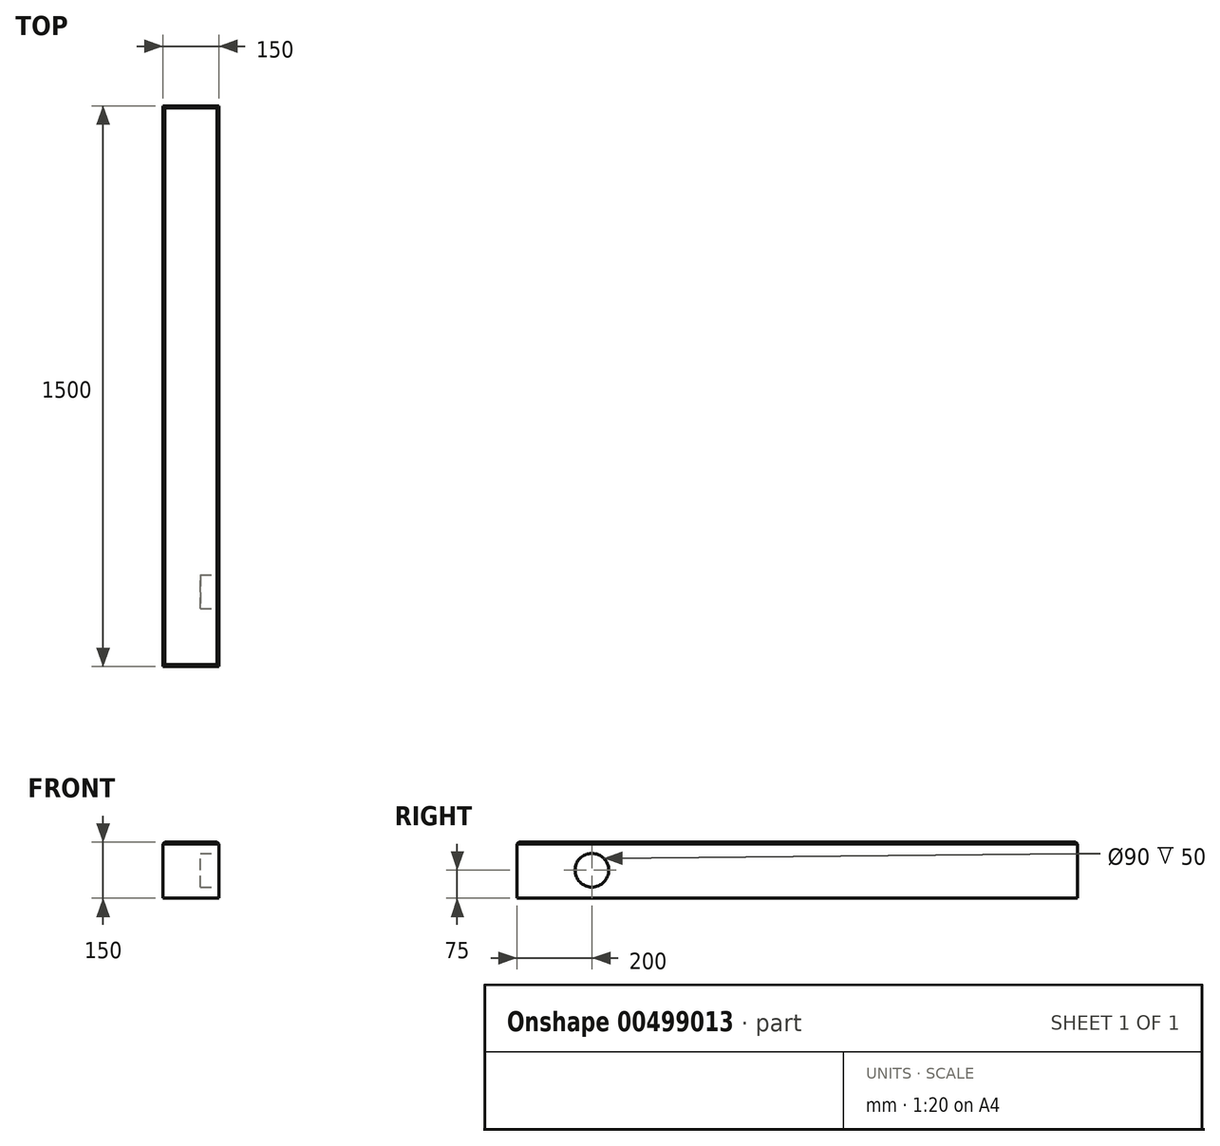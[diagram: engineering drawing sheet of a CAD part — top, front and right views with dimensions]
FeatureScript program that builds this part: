
annotation { "Feature Type Name" : "Feature", "Feature Type Description" : "" }
export const myFeature = defineFeature(function(context is Context, id is Id, definition is map)
    precondition{}
    {
        {
            var Q0;
            Q0=qCreatedBy(makeId("Front.planeOp"),FACE);
            var sketch = newSketch(context, id + "F0", { "sketchPlane" : qUnion([Q0])});
            skLineSegment(sketch, "E0.bottom", {"start": v(-75, 75) * mm, "end": v(75, 75) * mm});
            skLineSegment(sketch, "E0.top", {"start": v(-75, -75) * mm, "end": v(75, -75) * mm});
            skLineSegment(sketch, "E0.left", {"start": v(-75, 75) * mm, "end": v(-75, -75) * mm});
            skLineSegment(sketch, "E0.right", {"start": v(75, 75) * mm, "end": v(75, -75) * mm});
            skPoint(sketch, "E0.middle", {"position": v(0, 0) * mm});
            skSolve(sketch);
        }
        {
            var Q0;
            Q0 = qSketchRegion(id + "F0", true);
            extrude(context, id + "F1", {"entities" : qUnion([Q0]), "endBound" : BoundingType.SYMMETRIC, "depth" : 1500 * mm});
        }
        {
            var Q0;
            Q0=makeQuery(id+"F1.opExtrude","SWEPT_FACE",FACE,{"disambiguationData":[OSD([sQuery(id+"F0.wireOp",EDGE,"E0.bottom")])]});
            chamfer(context, id + "F2", {"entities" : qUnion([Q0]), "width" : 5 * mm, "tangentPropagation" : true});
        }
        {
            var Q0;
            Q0=makeQuery(id+"F1.opExtrude","SWEPT_FACE",FACE,{"disambiguationData":[OSD([sQuery(id+"F0.wireOp",EDGE,"E0.right")])]});
            var sketch = newSketch(context, id + "F3", { "sketchPlane" : qUnion([Q0])});
            skCircle(sketch, "E1", {"center": v(-550, 0) * mm, "radius": 45 * mm});
            skSolve(sketch);
        }
        {
            var Q0;
            Q0 = qSketchRegion(id + "F3", true);
            extrude(context, id + "F4", {"entities" : qUnion([Q0]), "operationType" : NewBodyOperationType.REMOVE, "oppositeDirection" : true, "depth" : 50 * mm});
        }
    });
